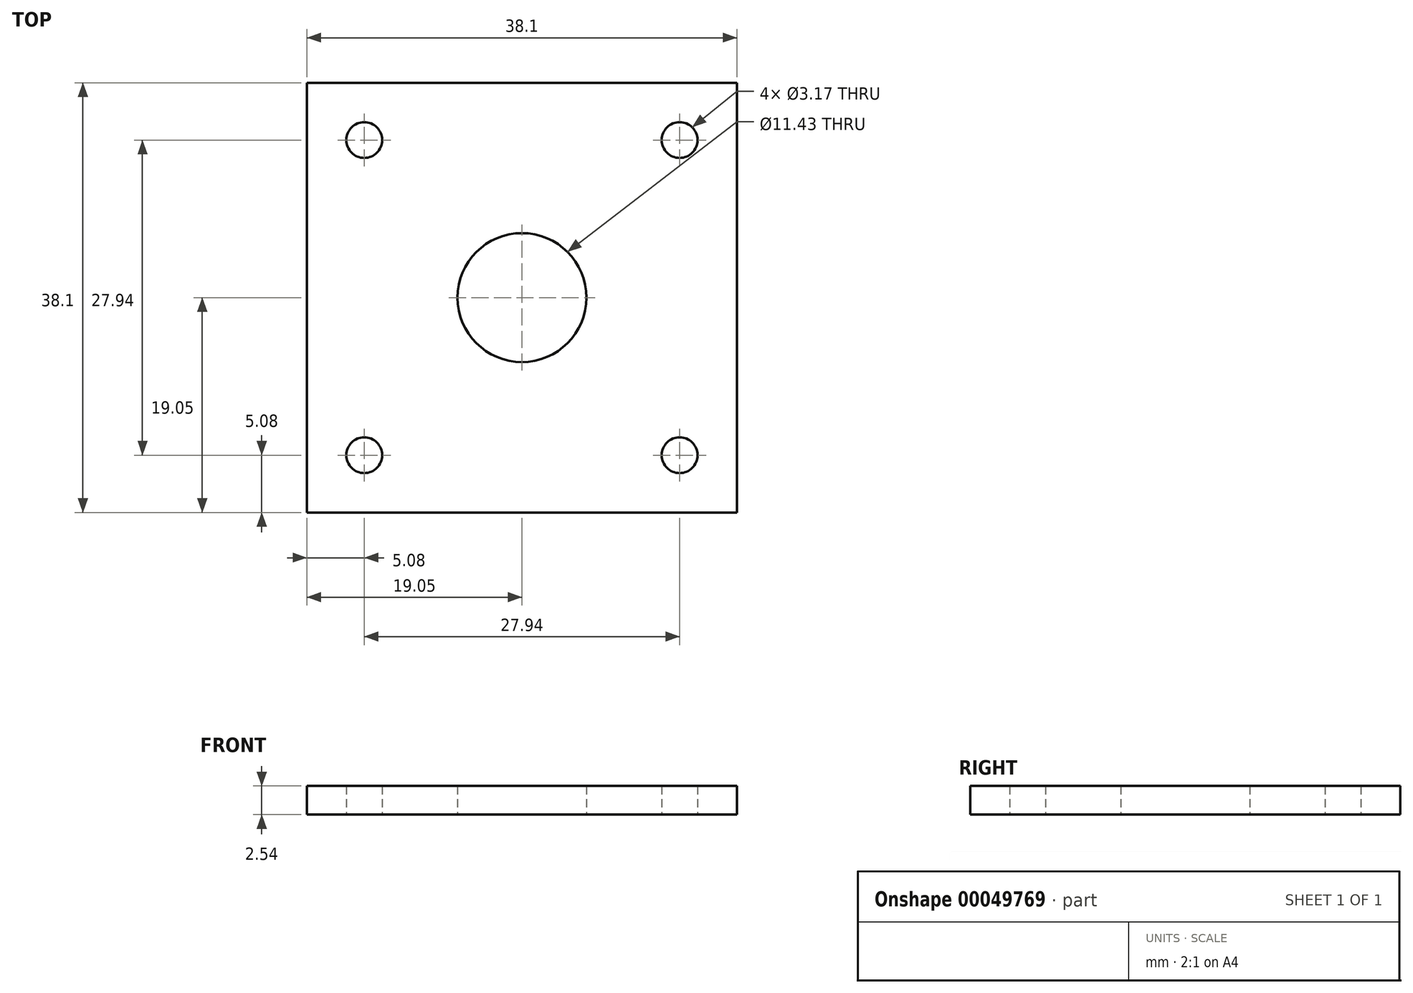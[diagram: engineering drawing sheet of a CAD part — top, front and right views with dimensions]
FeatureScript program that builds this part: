
annotation { "Feature Type Name" : "Feature", "Feature Type Description" : "" }
export const myFeature = defineFeature(function(context is Context, id is Id, definition is map)
    precondition{}
    {
        {
            var Q0;
            Q0=qCreatedBy(makeId("Top.planeOp"),FACE);
            var sketch = newSketch(context, id + "F0", { "sketchPlane" : qUnion([Q0])});
            skLineSegment(sketch, "E0.rect.bottom", {"start": v(19.05, -19.05) * mm, "end": v(-19.05, -19.05) * mm});
            skLineSegment(sketch, "E0.rect.top", {"start": v(19.05, 19.05) * mm, "end": v(-19.05, 19.05) * mm});
            skLineSegment(sketch, "E0.rect.left", {"start": v(19.05, -19.05) * mm, "end": v(19.05, 19.05) * mm});
            skLineSegment(sketch, "E0.rect.right", {"start": v(-19.05, -19.05) * mm, "end": v(-19.05, 19.05) * mm});
            skPoint(sketch, "E0.rect.middle", {"position": v(0, 0) * mm});
            skSolve(sketch);
        }
        {
            var Q0;
            Q0=qSketchRegion(id+"F0",true);
            extrude(context, id + "F1", {"entities" : qUnion([Q0]), "depth" : 2.54 * mm});
        }
        {
            var Q0;
            Q0=qCreatedBy(makeId("Top.planeOp"),FACE);
            var sketch = newSketch(context, id + "F2", { "sketchPlane" : qUnion([Q0])});
            skCircle(sketch, "E1", {"center": v(0, 0) * mm, "radius": 5.72 * mm});
            skSolve(sketch);
        }
        {
            var Q0;
            Q0=qSketchRegion(id+"F2",true);
            extrude(context, id + "F3", {"entities" : qUnion([Q0]), "operationType" : NewBodyOperationType.REMOVE, "depth" : 25.4 * mm});
        }
        {
            var Q0;
            Q0=qCreatedBy(makeId("Top.planeOp"),FACE);
            var sketch = newSketch(context, id + "F4", { "sketchPlane" : qUnion([Q0])});
            skCircle(sketch, "E2", {"center": v(13.97, 13.97) * mm, "radius": 1.59 * mm});
            skSolve(sketch);
        }
        {
            var Q0;
            Q0=qSketchRegion(id+"F4",true);
            extrude(context, id + "F5", {"entities" : qUnion([Q0]), "operationType" : NewBodyOperationType.REMOVE, "depth" : 25.4 * mm});
        }
        {
            var Q0;
            Q0=makeQuery(id+"F1.opExtrude","SWEPT_BODY",BODY,{"disambiguationData":[OSD([sQuery(id+"F0.wireOp",EDGE,"E0.rect.bottom"),sQuery(id+"F0.wireOp",EDGE,"E0.rect.top"),sQuery(id+"F0.wireOp",EDGE,"E0.rect.left"),sQuery(id+"F0.wireOp",EDGE,"E0.rect.right")])]});
            var Q1;
            Q1=qCreatedBy(makeId("Right.planeOp"),FACE);
            mirror(context, id + "F6", {"operationType" : NewBodyOperationType.INTERSECT, "entities" : qUnion([Q0]), "mirrorPlane" : qUnion([Q1])});
        }
        {
            var Q0;
            Q0=makeQuery(id+"F1.opExtrude","SWEPT_BODY",BODY,{"disambiguationData":[OSD([sQuery(id+"F0.wireOp",EDGE,"E0.rect.bottom"),sQuery(id+"F0.wireOp",EDGE,"E0.rect.top"),sQuery(id+"F0.wireOp",EDGE,"E0.rect.left"),sQuery(id+"F0.wireOp",EDGE,"E0.rect.right")])]});
            var Q1;
            Q1=qCreatedBy(makeId("Front.planeOp"),FACE);
            mirror(context, id + "F7", {"operationType" : NewBodyOperationType.INTERSECT, "entities" : qUnion([Q0]), "mirrorPlane" : qUnion([Q1])});
        }
    });
